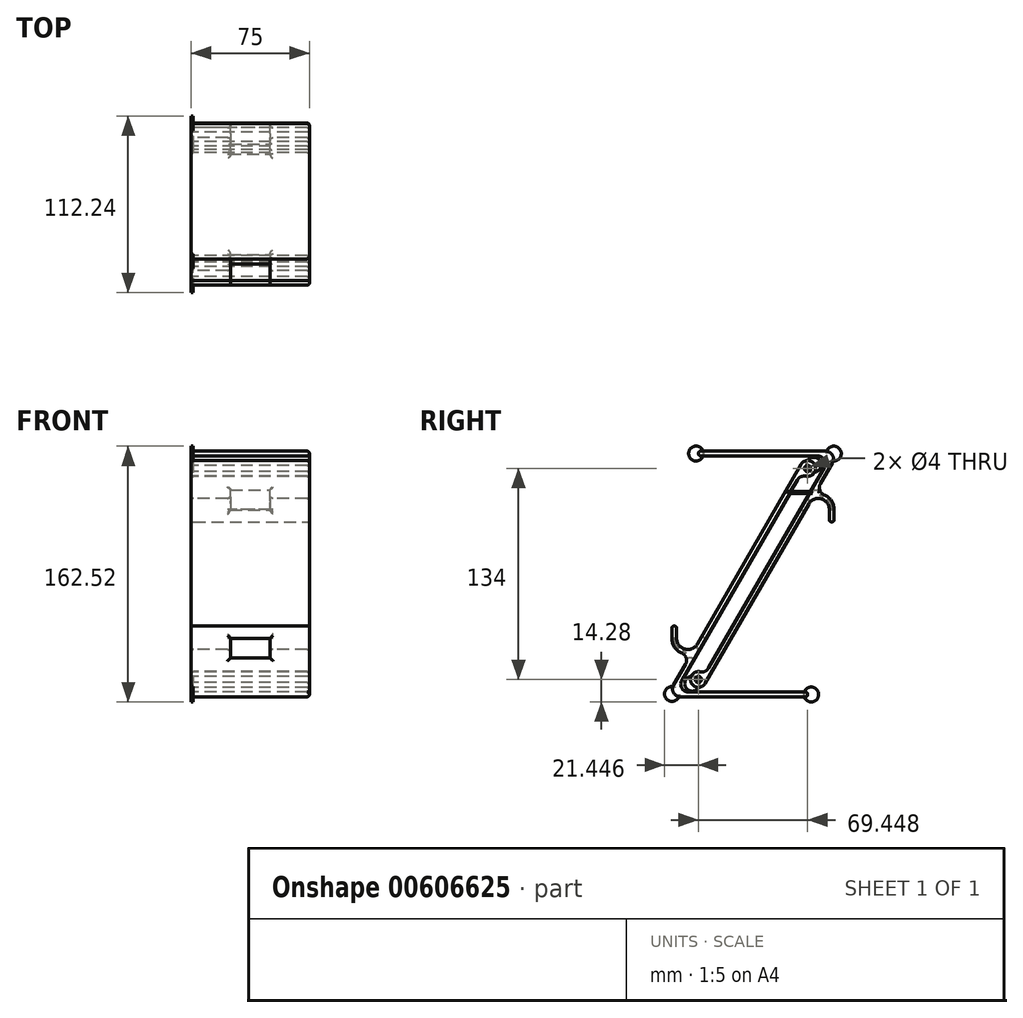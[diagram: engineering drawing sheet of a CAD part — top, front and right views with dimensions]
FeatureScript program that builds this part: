
annotation { "Feature Type Name" : "Feature", "Feature Type Description" : "" }
export const myFeature = defineFeature(function(context is Context, id is Id, definition is map)
    precondition{}
    {
        {
            var Q0;
            Q0=qCreatedBy(makeId("Right.planeOp"),FACE);
            var sketch = newSketch(context, id + "F0", { "sketchPlane" : qUnion([Q0])});
            skLineSegment(sketch, "E0.2", {"start": v(-43.49, -30) * mm, "end": v(-43.49, -38) * mm});
            skArc(sketch, "E0.4", {"start": v(-43.49, -38) * mm, "mid": v(-41.8, -43.57) * mm, "end": v(-37.29, -47.25) * mm});
            skLineSegment(sketch, "E1.2", {"start": v(-40.49, -30) * mm, "end": v(-40.49, -38) * mm});
            skLineSegment(sketch, "E1.3", {"start": v(-27.42, -41.5) * mm, "end": v(38.4, 72.5) * mm});
            skArc(sketch, "E2.filletArc", {"start": v(-40.49, -38) * mm, "mid": v(-35.3, -44.76) * mm, "end": v(-27.42, -41.5) * mm});
            skLineSegment(sketch, "E3", {"start": v(-43.49, -30) * mm, "end": v(-40.49, -30) * mm});
            skLineSegment(sketch, "E4", {"start": v(-42.44, -67.5) * mm, "end": v(-34.86, -54.37) * mm});
            skLineSegment(sketch, "E5.bottom", {"start": v(-38.1, -75) * mm, "end": v(42.72, -75) * mm});
            skLineSegment(sketch, "E5.top", {"start": v(-32.9, -72) * mm, "end": v(42.72, -72) * mm});
            skLineSegment(sketch, "E5.right", {"start": v(42.72, -75) * mm, "end": v(42.72, -72) * mm});
            skLineSegment(sketch, "E6", {"start": v(-37.24, -64.5) * mm, "end": v(36.22, 62.74) * mm});
            skPoint(sketch, "E7", {"position": v(0, 0) * mm});
            skArc(sketch, "E8", {"start": v(38.4, 72.5) * mm, "mid": v(47.3, 72.01) * mm, "end": v(41.64, 65.12) * mm});
            skPoint(sketch, "E9.visualSharp", {"position": v(-31, -47.68) * mm});
            skArc(sketch, "E9.filletArc", {"start": v(-34.86, -54.37) * mm, "mid": v(-34.45, -50.26) * mm, "end": v(-37.29, -47.25) * mm});
            skArc(sketch, "E10.filletArc", {"start": v(-37.24, -64.5) * mm, "mid": v(-37.24, -69.5) * mm, "end": v(-32.9, -72) * mm});
            skArc(sketch, "E11.filletArc", {"start": v(-42.44, -67.5) * mm, "mid": v(-42.44, -72.5) * mm, "end": v(-38.1, -75) * mm});
            skArc(sketch, "E12", {"start": v(41.64, 65.12) * mm, "mid": v(38.54, 64.82) * mm, "end": v(36.22, 62.74) * mm});
            skCircle(sketch, "E13", {"center": v(42.72, 70) * mm, "radius": 2 * mm});
            skSolve(sketch);
        }
        {
            var Q0;
            Q0=qSketchRegion(id+"F0",true);
            extrude(context, id + "F1", {"entities" : qUnion([Q0]), "endBound" : BoundingType.SYMMETRIC, "depth" : 75 * mm, "offsetDistance" : 25 * mm});
        }
        {
            var Q0;
            Q0=makeQuery(id+"F1.opExtrude","SWEPT_FACE",FACE,{"disambiguationData":[OSD([sQuery(id+"F0.wireOp",EDGE,"E0.2")])]});
            var sketch = newSketch(context, id + "F2", { "sketchPlane" : qUnion([Q0])});
            skLineSegment(sketch, "E14.bottom", {"start": v(-12.5, -38) * mm, "end": v(12.5, -38) * mm});
            skLineSegment(sketch, "E14.top", {"start": v(-12.5, -50.25) * mm, "end": v(12.5, -50.25) * mm});
            skLineSegment(sketch, "E14.left", {"start": v(-12.5, -38) * mm, "end": v(-12.5, -50.25) * mm});
            skLineSegment(sketch, "E14.right", {"start": v(12.5, -38) * mm, "end": v(12.5, -50.25) * mm});
            skSolve(sketch);
        }
        {
            var Q0;
            Q0=qSketchRegion(id+"F2",true);
            extrude(context, id + "F3", {"entities" : qUnion([Q0]), "operationType" : NewBodyOperationType.REMOVE, "oppositeDirection" : true, "depth" : 25 * mm, "offsetDistance" : 25 * mm});
        }
        {
            var Q0;
            Q0=makeQuery(id+"F1.opExtrude","SWEPT_FACE",FACE,{"disambiguationData":[OSD([sQuery(id+"F0.wireOp",EDGE,"E3")])]});
            var Q1;
            Q1=makeQuery(id+"F1.opExtrude","CAP_FACE",FACE,{"disambiguationData":[OSD([sQuery(id+"F0.wireOp",EDGE,"E0.2"),sQuery(id+"F0.wireOp",EDGE,"E0.4"),sQuery(id+"F0.wireOp",EDGE,"E1.2"),sQuery(id+"F0.wireOp",EDGE,"E1.3"),sQuery(id+"F0.wireOp",EDGE,"E2.filletArc"),sQuery(id+"F0.wireOp",EDGE,"E3"),sQuery(id+"F0.wireOp",EDGE,"OJqH4mra-1SRE-s8op-VV3v-gDYp8EEXXtRn"),sQuery(id+"F0.wireOp",EDGE,"E4"),sQuery(id+"F0.wireOp",EDGE,"E5.bottom"),sQuery(id+"F0.wireOp",EDGE,"E5.top"),sQuery(id+"F0.wireOp",EDGE,"E5.right"),sQuery(id+"F0.wireOp",EDGE,"E6"),sQuery(id+"F0.wireOp",EDGE,"E8"),sQuery(id+"F0.wireOp",EDGE,"jVerfQlz-GGoS-WxWe-SnGt-XEWwIJdHr9bm"),sQuery(id+"F0.wireOp",EDGE,"E9.filletArc"),sQuery(id+"F0.wireOp",EDGE,"E10.filletArc"),sQuery(id+"F0.wireOp",EDGE,"E11.filletArc")])],"isStart":false});
            var Q2;
            Q2=makeQuery(id+"F1.opExtrude","CAP_FACE",FACE,{"disambiguationData":[OSD([sQuery(id+"F0.wireOp",EDGE,"E0.2"),sQuery(id+"F0.wireOp",EDGE,"E0.4"),sQuery(id+"F0.wireOp",EDGE,"E1.2"),sQuery(id+"F0.wireOp",EDGE,"E1.3"),sQuery(id+"F0.wireOp",EDGE,"E2.filletArc"),sQuery(id+"F0.wireOp",EDGE,"E3"),sQuery(id+"F0.wireOp",EDGE,"OJqH4mra-1SRE-s8op-VV3v-gDYp8EEXXtRn"),sQuery(id+"F0.wireOp",EDGE,"E4"),sQuery(id+"F0.wireOp",EDGE,"E5.bottom"),sQuery(id+"F0.wireOp",EDGE,"E5.top"),sQuery(id+"F0.wireOp",EDGE,"E5.right"),sQuery(id+"F0.wireOp",EDGE,"E6"),sQuery(id+"F0.wireOp",EDGE,"E8"),sQuery(id+"F0.wireOp",EDGE,"jVerfQlz-GGoS-WxWe-SnGt-XEWwIJdHr9bm"),sQuery(id+"F0.wireOp",EDGE,"E9.filletArc"),sQuery(id+"F0.wireOp",EDGE,"E10.filletArc"),sQuery(id+"F0.wireOp",EDGE,"E11.filletArc")])],"isStart":true});
            var Q3;
            Q3=makeQuery(id+"F1.opExtrude","SWEPT_FACE",FACE,{"disambiguationData":[OSD([sQuery(id+"F0.wireOp",EDGE,"E5.right")])]});
            var Q4;
            Q4=makeQuery(id+"F1.opExtrude","SWEPT_EDGE",EDGE,{"disambiguationData":[OSD([sQuery(id+"F0.wireOp",EDGE,"OJqH4mra-1SRE-s8op-VV3v-gDYp8EEXXtRn"),sQuery(id+"F0.wireOp",EDGE,"E8")])]});
            var Q5;
            Q5=makeQuery(id+"F1.opExtrude","SWEPT_EDGE",EDGE,{"disambiguationData":[OSD([sQuery(id+"F0.wireOp",EDGE,"OJqH4mra-1SRE-s8op-VV3v-gDYp8EEXXtRn"),sQuery(id+"F0.wireOp",EDGE,"jVerfQlz-GGoS-WxWe-SnGt-XEWwIJdHr9bm")])]});
            fillet(context, id + "F4", {"entities" : qUnion([Q0, Q1, Q2, Q3, Q4, Q5]), "radius" : 1.5 * mm, "tangentPropagation" : true, "allowEdgeOverflow" : false});
        }
        {
            var Q0;
            Q0=makeQuery(id+"F3.boolean.opBoolean","INTERSECT",EDGE,{"derivedFrom":[makeQuery(id+"F1.opExtrude","SWEPT_FACE",FACE,{"disambiguationData":[OSD([sQuery(id+"F0.wireOp",EDGE,"E9.filletArc")])]}),makeQuery(id+"F3.opExtrude","SWEPT_FACE",FACE,{"disambiguationData":[OSD([sQuery(id+"F2.wireOp",EDGE,"E14.top")])]})]});
            var Q1;
            Q1=makeQuery(id+"F3.boolean.opBoolean","INTERSECT",EDGE,{"derivedFrom":[makeQuery(id+"F1.opExtrude","SWEPT_FACE",FACE,{"disambiguationData":[OSD([sQuery(id+"F0.wireOp",EDGE,"E0.4")])]}),makeQuery(id+"F3.opExtrude","SWEPT_FACE",FACE,{"disambiguationData":[OSD([sQuery(id+"F2.wireOp",EDGE,"E14.right")])]})]});
            var Q2;
            Q2=makeQuery(id+"F3.boolean.opBoolean","INTERSECT",EDGE,{"derivedFrom":[makeQuery(id+"F1.opExtrude","SWEPT_FACE",FACE,{"disambiguationData":[OSD([sQuery(id+"F0.wireOp",EDGE,"E0.4")])]}),makeQuery(id+"F3.opExtrude","SWEPT_FACE",FACE,{"disambiguationData":[OSD([sQuery(id+"F2.wireOp",EDGE,"E14.left")])]})]});
            var Q3;
            Q3=makeQuery(id+"F3.boolean.opBoolean","MERGE",EDGE,{"derivedFrom":[makeQuery(id+"F1.opExtrude","SWEPT_EDGE",EDGE,{"disambiguationData":[OSD([sQuery(id+"F0.wireOp",EDGE,"E0.2"),sQuery(id+"F0.wireOp",EDGE,"E0.4")])]}),makeQuery(id+"F3.opExtrude","CAP_EDGE",EDGE,{"disambiguationData":[OSD([sQuery(id+"F2.wireOp",EDGE,"E14.bottom")])],"isStart":true})]});
            fillet(context, id + "F5", {"entities" : qUnion([Q0, Q1, Q2, Q3]), "radius" : 2 * mm, "tangentPropagation" : true, "allowEdgeOverflow" : false});
        }
        {
            var Q0;
            Q0=makeQuery(id+"F3.boolean.opBoolean","INTERSECT",EDGE,{"derivedFrom":[makeQuery(id+"F1.opExtrude","SWEPT_FACE",FACE,{"disambiguationData":[OSD([sQuery(id+"F0.wireOp",EDGE,"E1.3")])]}),makeQuery(id+"F3.opExtrude","SWEPT_FACE",FACE,{"disambiguationData":[OSD([sQuery(id+"F2.wireOp",EDGE,"E14.bottom")])]})]});
            var Q1;
            Q1=makeQuery(id+"F3.boolean.opBoolean","INTERSECT",EDGE,{"derivedFrom":[makeQuery(id+"F1.opExtrude","SWEPT_FACE",FACE,{"disambiguationData":[OSD([sQuery(id+"F0.wireOp",EDGE,"E2.filletArc")])]}),makeQuery(id+"F3.opExtrude","SWEPT_FACE",FACE,{"disambiguationData":[OSD([sQuery(id+"F2.wireOp",EDGE,"E14.left")])]})]});
            var Q2;
            Q2=makeQuery(id+"F3.boolean.opBoolean","INTERSECT",EDGE,{"derivedFrom":[makeQuery(id+"F1.opExtrude","SWEPT_FACE",FACE,{"disambiguationData":[OSD([sQuery(id+"F0.wireOp",EDGE,"E2.filletArc")])]}),makeQuery(id+"F3.opExtrude","SWEPT_FACE",FACE,{"disambiguationData":[OSD([sQuery(id+"F2.wireOp",EDGE,"E14.right")])]})]});
            fillet(context, id + "F6", {"entities" : qUnion([Q0, Q1, Q2]), "radius" : 2 * mm, "tangentPropagation" : true, "allowEdgeOverflow" : false});
        }
        {
            var Q0;
            Q0=makeQuery(id+"F3.boolean.opBoolean","INTERSECT",EDGE,{"derivedFrom":[makeQuery(id+"F1.opExtrude","SWEPT_FACE",FACE,{"disambiguationData":[OSD([sQuery(id+"F0.wireOp",EDGE,"E6")])]}),makeQuery(id+"F3.opExtrude","SWEPT_FACE",FACE,{"disambiguationData":[OSD([sQuery(id+"F2.wireOp",EDGE,"E14.right")])]})]});
            var Q1;
            Q1=makeQuery(id+"F3.boolean.opBoolean","INTERSECT",EDGE,{"derivedFrom":[makeQuery(id+"F1.opExtrude","SWEPT_FACE",FACE,{"disambiguationData":[OSD([sQuery(id+"F0.wireOp",EDGE,"E6")])]}),makeQuery(id+"F3.opExtrude","SWEPT_FACE",FACE,{"disambiguationData":[OSD([sQuery(id+"F2.wireOp",EDGE,"E14.top")])]})]});
            var Q2;
            Q2=makeQuery(id+"F6.opFillet","BLEND_EDGE",EDGE,{"blendedFrom":[makeQuery(id+"F3.boolean.opBoolean","INTERSECT",EDGE,{"derivedFrom":[makeQuery(id+"F1.opExtrude","SWEPT_FACE",FACE,{"disambiguationData":[OSD([sQuery(id+"F0.wireOp",EDGE,"E1.3")])]}),makeQuery(id+"F3.opExtrude","SWEPT_FACE",FACE,{"disambiguationData":[OSD([sQuery(id+"F2.wireOp",EDGE,"E14.bottom")])]})]}),makeQuery(id+"F1.opExtrude","SWEPT_FACE",FACE,{"disambiguationData":[OSD([sQuery(id+"F0.wireOp",EDGE,"E6")])]})],"blendedInto":[makeQuery(id+"F1.opExtrude","SWEPT_FACE",FACE,{"disambiguationData":[OSD([sQuery(id+"F0.wireOp",EDGE,"E6")])]})]});
            var Q3;
            Q3=makeQuery(id+"F3.boolean.opBoolean","INTERSECT",EDGE,{"derivedFrom":[makeQuery(id+"F1.opExtrude","SWEPT_FACE",FACE,{"disambiguationData":[OSD([sQuery(id+"F0.wireOp",EDGE,"E6")])]}),makeQuery(id+"F3.opExtrude","SWEPT_FACE",FACE,{"disambiguationData":[OSD([sQuery(id+"F2.wireOp",EDGE,"E14.left")])]})]});
            fillet(context, id + "F7", {"entities" : qUnion([Q0, Q1, Q2, Q3]), "radius" : 1.4 * mm, "tangentPropagation" : true, "allowEdgeOverflow" : false});
        }
        {
            var Q0;
            Q0=qCreatedBy(makeId("Front.planeOp"),FACE);
            cPlane(context, id + "F8", {"entities" : qUnion([Q0]), "cplaneType" : CPlaneType.OFFSET, "offset" : 8 * mm, "oppositeDirection" : true, "width" : 150 * mm, "height" : 150 * mm});
        }
        {
            var Q0;
            Q0=qCreatedBy(id+"F8.planeOp",FACE);
            var sketch = newSketch(context, id + "F9", { "sketchPlane" : qUnion([Q0])});
            skLineSegment(sketch, "E15", {"start": v(0, 3) * mm, "end": v(46.47, 3) * mm, "construction": true});
            skSolve(sketch);
        }
        {
            var Q0;
            Q0=makeQuery(id+"F1.opExtrude","SWEPT_BODY",BODY,{"disambiguationData":[OSD([sQuery(id+"F0.wireOp",EDGE,"E0.2"),sQuery(id+"F0.wireOp",EDGE,"E0.4"),sQuery(id+"F0.wireOp",EDGE,"E1.2"),sQuery(id+"F0.wireOp",EDGE,"E1.3"),sQuery(id+"F0.wireOp",EDGE,"E2.filletArc"),sQuery(id+"F0.wireOp",EDGE,"E3"),sQuery(id+"F0.wireOp",EDGE,"E4"),sQuery(id+"F0.wireOp",EDGE,"E5.bottom"),sQuery(id+"F0.wireOp",EDGE,"E5.top"),sQuery(id+"F0.wireOp",EDGE,"E5.right"),sQuery(id+"F0.wireOp",EDGE,"E6"),sQuery(id+"F0.wireOp",EDGE,"E8"),sQuery(id+"F0.wireOp",EDGE,"E9.filletArc"),sQuery(id+"F0.wireOp",EDGE,"E10.filletArc"),sQuery(id+"F0.wireOp",EDGE,"E11.filletArc"),sQuery(id+"F0.wireOp",EDGE,"E12"),sQuery(id+"F0.wireOp",EDGE,"E13")])]});
            var Q1;
            Q1=sQuery(id+"F9.wireOp",EDGE,"E15");
            circularPattern(context, id + "F10", {"entities" : qUnion([Q0]), "axis" : qUnion([Q1]), "angle" : 360 * degree, "instanceCount" : 2, "equalSpace" : true});
        }
        {
            var Q0;
            Q0=makeQuery(id+"F10.opPattern","COPY",FACE,{"derivedFrom":makeQuery(id+"F4.opFillet","SPLIT",FACE,{"disambiguationData":[OD(1.0)],"derivedFrom":makeQuery(id+"F1.opExtrude","CAP_FACE",FACE,{"disambiguationData":[OSD([sQuery(id+"F0.wireOp",EDGE,"E0.2"),sQuery(id+"F0.wireOp",EDGE,"E0.4"),sQuery(id+"F0.wireOp",EDGE,"E1.2"),sQuery(id+"F0.wireOp",EDGE,"E1.3"),sQuery(id+"F0.wireOp",EDGE,"E2.filletArc"),sQuery(id+"F0.wireOp",EDGE,"E3"),sQuery(id+"F0.wireOp",EDGE,"E4"),sQuery(id+"F0.wireOp",EDGE,"E5.bottom"),sQuery(id+"F0.wireOp",EDGE,"E5.top"),sQuery(id+"F0.wireOp",EDGE,"E5.right"),sQuery(id+"F0.wireOp",EDGE,"E6"),sQuery(id+"F0.wireOp",EDGE,"E8"),sQuery(id+"F0.wireOp",EDGE,"E9.filletArc"),sQuery(id+"F0.wireOp",EDGE,"E10.filletArc"),sQuery(id+"F0.wireOp",EDGE,"E11.filletArc"),sQuery(id+"F0.wireOp",EDGE,"E12"),sQuery(id+"F0.wireOp",EDGE,"E13")])],"isStart":false})}),"instanceName":"1"});
            var sketch = newSketch(context, id + "F11", { "sketchPlane" : qUnion([Q0])});
            skLineSegment(sketch, "E16.bottom", {"start": v(29.76, 55.26) * mm, "end": v(49.76, 55.26) * mm});
            skLineSegment(sketch, "E16.top", {"start": v(29.76, 54.26) * mm, "end": v(49.76, 54.26) * mm});
            skLineSegment(sketch, "E16.left", {"start": v(29.76, 55.26) * mm, "end": v(29.76, 54.26) * mm});
            skLineSegment(sketch, "E16.right", {"start": v(49.76, 55.26) * mm, "end": v(49.76, 54.26) * mm});
            skSolve(sketch);
        }
        {
            var Q0;
            Q0=qSketchRegion(id+"F11",true);
            extrude(context, id + "F12", {"entities" : qUnion([Q0]), "operationType" : NewBodyOperationType.ADD, "oppositeDirection" : true, "depth" : 0.01 * mm, "offsetDistance" : 25 * mm});
        }
        {
            var Q0;
            Q0=makeQuery(id+"F10.opPattern","COPY",FACE,{"derivedFrom":makeQuery(id+"F4.opFillet","SPLIT",FACE,{"disambiguationData":[OD(2.0)],"derivedFrom":makeQuery(id+"F1.opExtrude","CAP_FACE",FACE,{"disambiguationData":[OSD([sQuery(id+"F0.wireOp",EDGE,"E0.2"),sQuery(id+"F0.wireOp",EDGE,"E0.4"),sQuery(id+"F0.wireOp",EDGE,"E1.2"),sQuery(id+"F0.wireOp",EDGE,"E1.3"),sQuery(id+"F0.wireOp",EDGE,"E2.filletArc"),sQuery(id+"F0.wireOp",EDGE,"E3"),sQuery(id+"F0.wireOp",EDGE,"E4"),sQuery(id+"F0.wireOp",EDGE,"E5.bottom"),sQuery(id+"F0.wireOp",EDGE,"E5.top"),sQuery(id+"F0.wireOp",EDGE,"E5.right"),sQuery(id+"F0.wireOp",EDGE,"E6"),sQuery(id+"F0.wireOp",EDGE,"E8"),sQuery(id+"F0.wireOp",EDGE,"E9.filletArc"),sQuery(id+"F0.wireOp",EDGE,"E10.filletArc"),sQuery(id+"F0.wireOp",EDGE,"E11.filletArc"),sQuery(id+"F0.wireOp",EDGE,"E12"),sQuery(id+"F0.wireOp",EDGE,"E13")])],"isStart":true})}),"instanceName":"1"});
            var sketch = newSketch(context, id + "F13", { "sketchPlane" : qUnion([Q0])});
            skCircle(sketch, "E17", {"center": v(-59.33, 79.46) * mm, "radius": 4.74 * mm});
            skCircle(sketch, "E18", {"center": v(-46.57, 72.33) * mm, "radius": 4.74 * mm});
            skCircle(sketch, "E19", {"center": v(28.15, 79.5) * mm, "radius": 4.74 * mm});
            skCircle(sketch, "E20", {"center": v(43.43, -73.21) * mm, "radius": 4.74 * mm});
            skCircle(sketch, "E21", {"center": v(30.63, -66.73) * mm, "radius": 4.74 * mm});
            skCircle(sketch, "E22", {"center": v(-44.98, -73.55) * mm, "radius": 4.74 * mm});
            skSolve(sketch);
        }
        {
            var Q0;
            Q0 = qSketchRegion(id + "F13", true);
            extrude(context, id + "F14", {"entities" : qUnion([Q0]), "operationType" : NewBodyOperationType.ADD, "oppositeDirection" : true, "depth" : 1 * mm, "offsetDistance" : 25 * mm});
        }
    });
